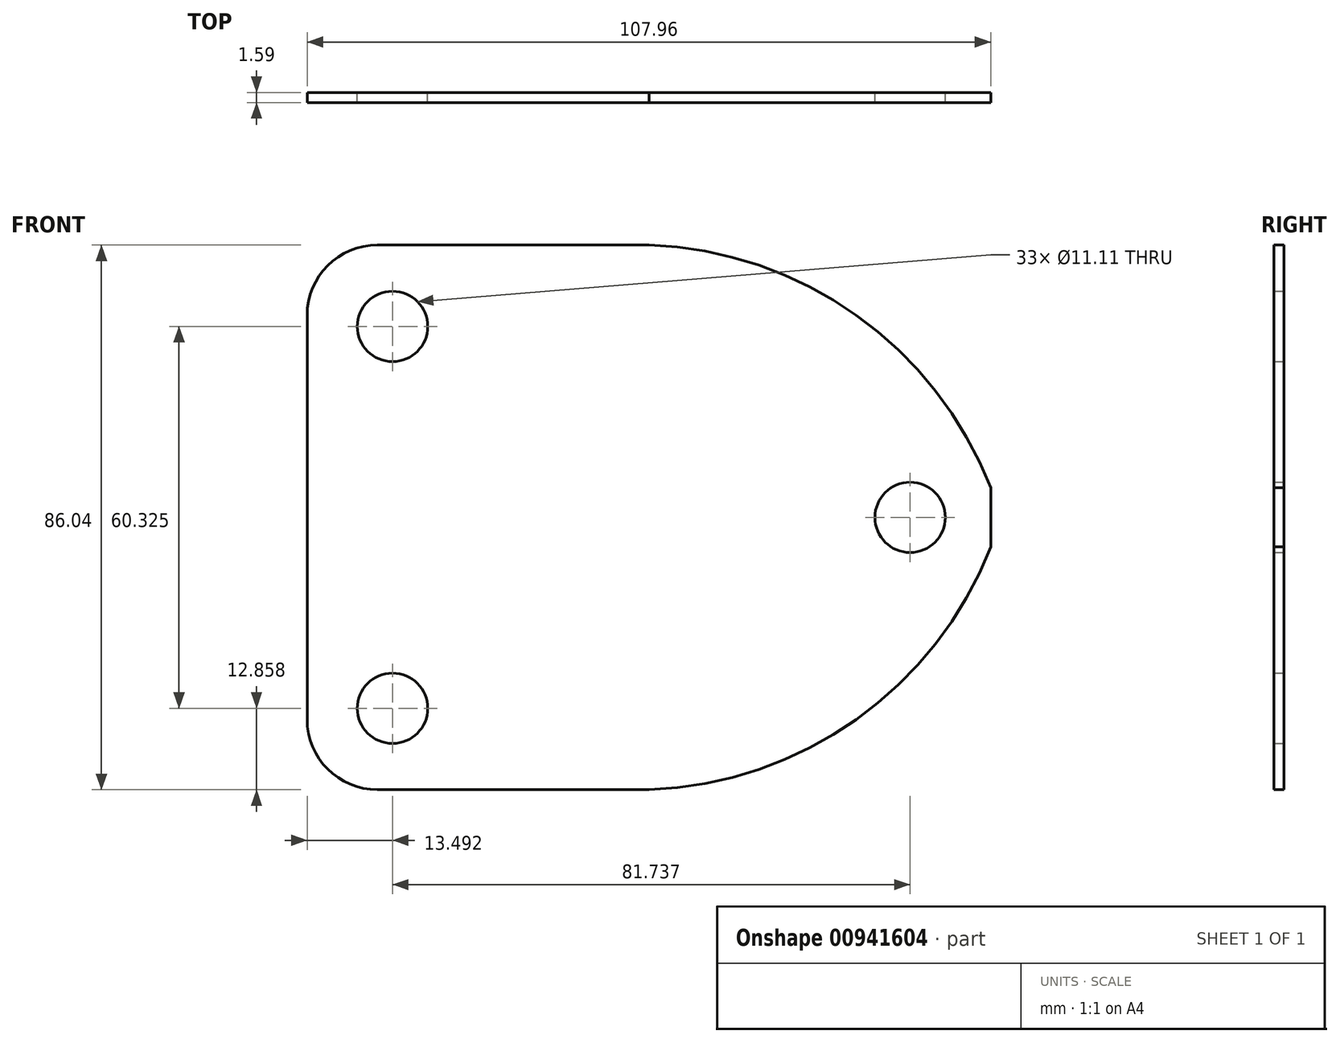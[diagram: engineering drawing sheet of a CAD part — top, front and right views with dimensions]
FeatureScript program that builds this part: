
annotation { "Feature Type Name" : "Feature", "Feature Type Description" : "" }
export const myFeature = defineFeature(function(context is Context, id is Id, definition is map)
    precondition{}
    {
        {
            var Q0;
            Q0=qCreatedBy(makeId("Front.planeOp"),FACE);
            var sketch = newSketch(context, id + "F0", { "sketchPlane" : qUnion([Q0])});
            skLineSegment(sketch, "E0.bottom", {"start": v(53.97, -43.02) * mm, "end": v(-53.98, -43.02) * mm});
            skLineSegment(sketch, "E0.top", {"start": v(53.98, 43.02) * mm, "end": v(-53.97, 43.02) * mm});
            skLineSegment(sketch, "E0.left", {"start": v(53.97, -43.02) * mm, "end": v(53.98, 43.02) * mm});
            skLineSegment(sketch, "E0.right", {"start": v(-53.98, -43.02) * mm, "end": v(-53.97, 43.02) * mm});
            skPoint(sketch, "E0.middle", {"position": v(0, 0) * mm});
            skSolve(sketch);
        }
        {
            var Q0;
            Q0 = qSketchRegion(id + "F0", true);
            extrude(context, id + "F1", {"entities" : qUnion([Q0]), "depth" : 1.59 * mm, "offsetDistance" : 25.4 * mm});
        }
        {
            var Q0;
            Q0=makeQuery(id+"F1.opExtrude","SWEPT_EDGE",EDGE,{"disambiguationData":[OSD([sQuery(id+"F0.wireOp",EDGE,"E0.top"),sQuery(id+"F0.wireOp",EDGE,"E0.right")])]});
            var Q1;
            Q1=makeQuery(id+"F1.opExtrude","SWEPT_EDGE",EDGE,{"disambiguationData":[OSD([sQuery(id+"F0.wireOp",EDGE,"E0.bottom"),sQuery(id+"F0.wireOp",EDGE,"E0.right")])]});
            fillet(context, id + "F2", {"entities" : qUnion([Q0, Q1]), "radius" : 11.1 * mm, "tangentPropagation" : true, "allowEdgeOverflow" : false});
        }
        {
            var Q0;
            Q0=qCreatedBy(makeId("Front.planeOp"),FACE);
            var sketch = newSketch(context, id + "F3", { "sketchPlane" : qUnion([Q0])});
            skCircle(sketch, "E1", {"center": v(-40.49, 30.16) * mm, "radius": 5.56 * mm});
            skCircle(sketch, "E2", {"center": v(-40.49, -30.16) * mm, "radius": 5.56 * mm});
            skCircle(sketch, "E3", {"center": v(41.25, 0) * mm, "radius": 5.56 * mm});
            skLineSegment(sketch, "E4", {"start": v(-40.49, -30.16) * mm, "end": v(-40.49, 0) * mm, "construction": true});
            skLineSegment(sketch, "E5", {"start": v(-40.49, 0) * mm, "end": v(-40.49, 30.16) * mm, "construction": true});
            skSolve(sketch);
        }
        {
            var Q0;
            Q0 = qSketchRegion(id + "F3", true);
            extrude(context, id + "F4", {"entities" : qUnion([Q0]), "operationType" : NewBodyOperationType.REMOVE, "endBound" : BoundingType.THROUGH_ALL, "depth" : 25.4 * mm, "offsetDistance" : 25.4 * mm});
        }
        {
            var Q0;
            Q0=qCreatedBy(makeId("Front.planeOp"),FACE);
            var sketch = newSketch(context, id + "F5", { "sketchPlane" : qUnion([Q0])});
            skLineSegment(sketch, "E6", {"start": v(0, -43.02) * mm, "end": v(0, 43.02) * mm, "construction": true});
            skArc(sketch, "E7", {"start": v(55.56, 0) * mm, "mid": v(34.72, 30.47) * mm, "end": v(0, 43.02) * mm});
            skArc(sketch, "E8", {"start": v(0, -43.02) * mm, "mid": v(34.72, -30.47) * mm, "end": v(55.56, 0) * mm});
            skLineSegment(sketch, "E9", {"start": v(0, 43.02) * mm, "end": v(73.44, 43.02) * mm});
            skLineSegment(sketch, "E10", {"start": v(73.44, 43.02) * mm, "end": v(73.44, -43.02) * mm});
            skLineSegment(sketch, "E11", {"start": v(73.44, -43.02) * mm, "end": v(0, -43.02) * mm});
            skSolve(sketch);
        }
        {
            var Q0;
            Q0 = qSketchRegion(id + "F5", true);
            extrude(context, id + "F6", {"entities" : qUnion([Q0]), "operationType" : NewBodyOperationType.REMOVE, "endBound" : BoundingType.THROUGH_ALL, "depth" : 25.4 * mm, "offsetDistance" : 25.4 * mm});
        }
    });
